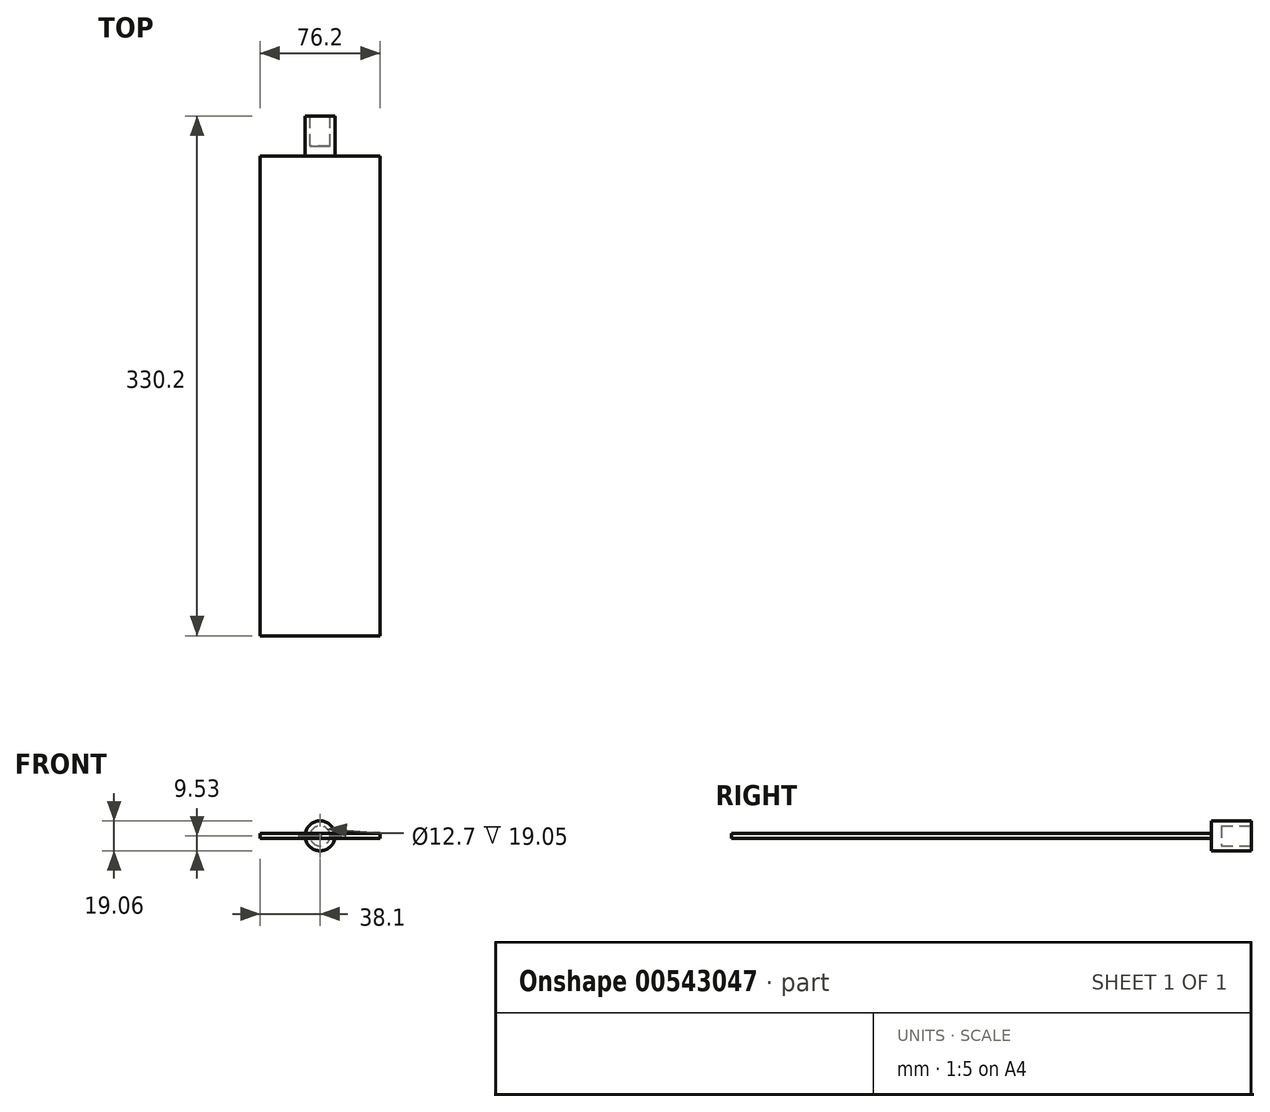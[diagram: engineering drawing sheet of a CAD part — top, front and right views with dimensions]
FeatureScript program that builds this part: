
annotation { "Feature Type Name" : "Feature", "Feature Type Description" : "" }
export const myFeature = defineFeature(function(context is Context, id is Id, definition is map)
    precondition{}
    {
        {
            var Q0;
            Q0=qCreatedBy(makeId("Front.planeOp"),FACE);
            var sketch = newSketch(context, id + "F0", { "sketchPlane" : qUnion([Q0])});
            skCircle(sketch, "E0", {"center": v(0, 0) * mm, "radius": 9.53 * mm});
            skSolve(sketch);
        }
        {
            var Q0;
            Q0 = qSketchRegion(id + "F0", true);
            extrude(context, id + "F1", {"entities" : qUnion([Q0]), "oppositeDirection" : true, "depth" : 25.4 * mm, "offsetDistance" : 25.4 * mm});
        }
        {
            var Q0;
            Q0=makeQuery(id+"F1.opExtrude","CAP_FACE",FACE,{"disambiguationData":[OSD([sQuery(id+"F0.wireOp",EDGE,"E0")])],"isStart":false});
            var sketch = newSketch(context, id + "F2", { "sketchPlane" : qUnion([Q0])});
            skCircle(sketch, "E1", {"center": v(0, 0) * mm, "radius": 6.35 * mm});
            skSolve(sketch);
        }
        {
            var Q0;
            Q0 = qSketchRegion(id + "F2", true);
            extrude(context, id + "F3", {"entities" : qUnion([Q0]), "operationType" : NewBodyOperationType.REMOVE, "oppositeDirection" : true, "depth" : 19.05 * mm, "offsetDistance" : 25.4 * mm});
        }
        {
            var Q0;
            Q0=qCreatedBy(makeId("Front.planeOp"),FACE);
            var sketch = newSketch(context, id + "F4", { "sketchPlane" : qUnion([Q0])});
            skLineSegment(sketch, "E2.bottom", {"start": v(-38.1, 1.59) * mm, "end": v(38.1, 1.59) * mm});
            skLineSegment(sketch, "E2.top", {"start": v(-38.1, -1.59) * mm, "end": v(38.1, -1.59) * mm});
            skLineSegment(sketch, "E2.left", {"start": v(-38.1, 1.59) * mm, "end": v(-38.1, -1.59) * mm});
            skLineSegment(sketch, "E2.right", {"start": v(38.1, 1.59) * mm, "end": v(38.1, -1.59) * mm});
            skLineSegment(sketch, "E3", {"start": v(38.1, 1.59) * mm, "end": v(-38.1, -1.59) * mm, "construction": true});
            skSolve(sketch);
        }
        {
            var Q0;
            Q0 = qSketchRegion(id + "F4", true);
            extrude(context, id + "F5", {"entities" : qUnion([Q0]), "operationType" : NewBodyOperationType.ADD, "depth" : 304.8 * mm, "offsetDistance" : 25.4 * mm});
        }
    });
